# Revit family: Drain-Trench_MultiDrain_AlfaSlot
name_source: partatom
category: Site
units: mm (PartAtom-declared; Revit-internal decimal feet)

## family parameters
Classification Number = 23.10.10.12
Cut with Voids When Loaded = No
Host = Face
Part Type = Normal
Round Connector Dimension = Use Diameter
Shared = No

## types (8) — shared parameters
ADA Compliant = Yes
Assembly Code = A1030600
Construction Details = http://www.arcat.com
Default Elevation = 0' - 0"
Description = MultiDrain Trench Drainage System - Alfa Slot as Specified
Keynote = 02600
Manufacturer = MultiDrain Systems
Manufacturer Fax = 704-508-1011
Manufacturer Website = http://www.multidrainsystems.com
Maximum Run = 0' - 0"
Model = Alfa Slot as Specified
No Slope Unit = Yes
Piping_Water Flow = 0 GPM
Product Data = http://www.arcat.com
Revision = R1_12_2013
Sales Information = http://www.multidrainsystems.com
Send Message = http://www.arcat.com
Specification = http://www.arcat.com
Trench Width = 0' - 2"
URL = http://www.multidrainsystems.com
zero-valued in all types: Expected Lifespan (Years), Maintenance Schedule (Months), Unit Slope_Percentage, Warranty Duration (Years)

## per-type parameters (varying)
| type | Grate Opening Width | Include HeelProof Cover | Pipe ID | Pipe OD | Uphill Trench Depth |
| 6in Pipe 0.5in Covered Gap | 0' - 0 1/2" | Yes | 0' - 6 1/16" | 0' - 6 5/8" | 0' - 8" |
| 4in Pipe 0.5in Covered Gap | 0' - 0 1/2" | Yes | 0' - 4 1/32" | 0' - 4 1/2" | 0' - 6" |
| 6in Pipe 0.25in Covered Gap | 0' - 0 1/4" | Yes | 0' - 6 1/16" | 0' - 6 5/8" | 0' - 8" |
| 4in Pipe 0.25in Covered Gap | 0' - 0 1/4" | Yes | 0' - 4 1/32" | 0' - 4 1/2" | 0' - 6" |
| 6in Pipe 0.5in Gap | 0' - 0 1/2" | No | 0' - 6 1/16" | 0' - 6 5/8" | 0' - 8" |
| 4in Pipe 0.5in Gap | 0' - 0 1/2" | No | 0' - 4 1/32" | 0' - 4 1/2" | 0' - 6" |
| 6in Pipe 0.25in Gap | 0' - 0 1/4" | No | 0' - 6 1/16" | 0' - 6 5/8" | 0' - 8" |
| 4in Pipe 0.25in Gap | 0' - 0 1/4" | No | 0' - 4 1/32" | 0' - 4 1/2" | 0' - 6" |

## geometry (parser evidence)
native form markers: Blend x6, Sweep x2
no freeform markers — native parametric forms only
